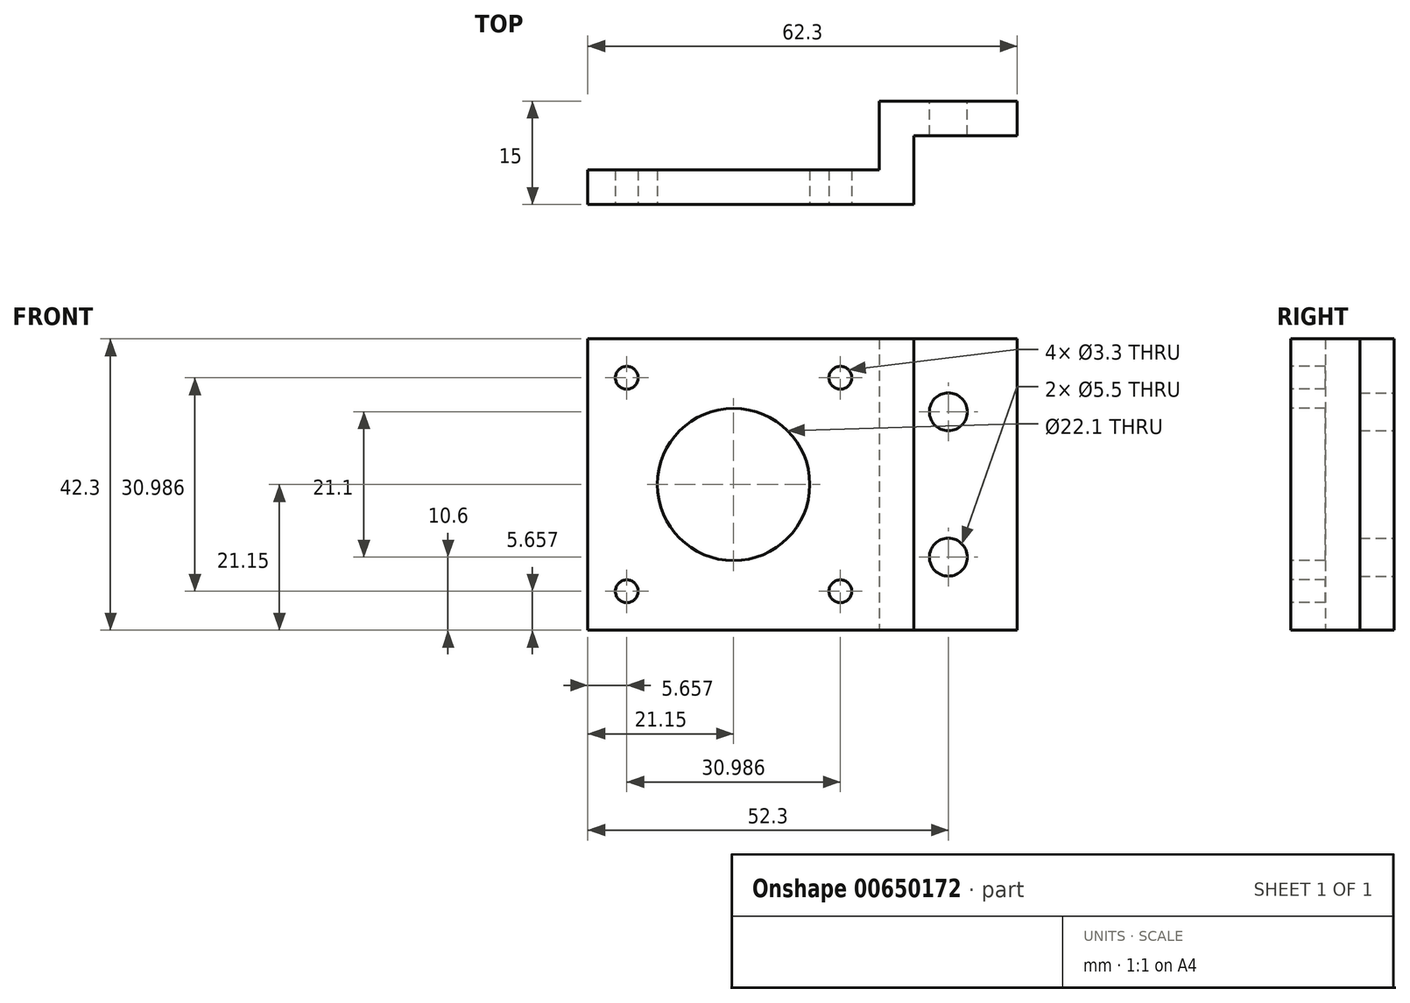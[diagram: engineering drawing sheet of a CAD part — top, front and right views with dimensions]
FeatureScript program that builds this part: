
annotation { "Feature Type Name" : "Feature", "Feature Type Description" : "" }
export const myFeature = defineFeature(function(context is Context, id is Id, definition is map)
    precondition{}
    {
        {
            var Q0;
            Q0=qCreatedBy(makeId("Front.planeOp"),FACE);
            var sketch = newSketch(context, id + "F0", { "sketchPlane" : qUnion([Q0])});
            skLineSegment(sketch, "E0.bottom", {"start": v(10, -21.15) * mm, "end": v(-10, -21.15) * mm});
            skLineSegment(sketch, "E0.top", {"start": v(10, 21.15) * mm, "end": v(-10, 21.15) * mm});
            skLineSegment(sketch, "E0.left", {"start": v(10, -21.15) * mm, "end": v(10, 21.15) * mm});
            skLineSegment(sketch, "E0.right", {"start": v(-10, -21.15) * mm, "end": v(-10, 21.15) * mm});
            skPoint(sketch, "E0.middle", {"position": v(0, 0) * mm});
            skPoint(sketch, "E1", {"position": v(0, 10.55) * mm});
            skPoint(sketch, "E2", {"position": v(0, -10.55) * mm});
            skSolve(sketch);
        }
        {
            var Q0;
            Q0=makeQuery(id+"F0.imprint","IMPRINT",FACE,{"disambiguationData":[TD([[makeQuery(id+"F0.imprint","IMPRINT",EDGE,{"derivedFrom":sQuery(id+"F0.wireOp",EDGE,"E0.bottom")}),-1.0]])]});
            extrude(context, id + "F1", {"entities" : qUnion([Q0]), "depth" : 5 * mm, "offsetDistance" : 25 * mm});
        }
        {
            var Q0;
            Q0=makeQuery(id+"F1.opExtrude","CAP_FACE",FACE,{"disambiguationData":[OSD([sQuery(id+"F0.wireOp",EDGE,"E0.bottom"),sQuery(id+"F0.wireOp",EDGE,"E0.top"),sQuery(id+"F0.wireOp",EDGE,"E0.left"),sQuery(id+"F0.wireOp",EDGE,"E0.right")])],"isStart":false});
            var sketch = newSketch(context, id + "F2", { "sketchPlane" : qUnion([Q0])});
            skLineSegment(sketch, "E3.bottom", {"start": v(-10, 21.15) * mm, "end": v(-5, 21.15) * mm});
            skLineSegment(sketch, "E3.top", {"start": v(-10, -21.15) * mm, "end": v(-5, -21.15) * mm});
            skLineSegment(sketch, "E3.left", {"start": v(-10, 21.15) * mm, "end": v(-10, -21.15) * mm});
            skLineSegment(sketch, "E3.right", {"start": v(-5, 21.15) * mm, "end": v(-5, -21.15) * mm});
            skSolve(sketch);
        }
        {
            var Q0;
            Q0=makeQuery(id+"F2.imprint","IMPRINT",FACE,{"disambiguationData":[TD([[makeQuery(id+"F2.imprint","IMPRINT",EDGE,{"derivedFrom":sQuery(id+"F2.wireOp",EDGE,"E3.bottom")}),1.0]])]});
            extrude(context, id + "F3", {"entities" : qUnion([Q0]), "operationType" : NewBodyOperationType.ADD, "depth" : 10 * mm, "offsetDistance" : 25 * mm});
        }
        {
            var Q0;
            Q0=makeQuery(id+"F3.boolean.opBoolean","MERGE",FACE,{"derivedFrom":[makeQuery(id+"F1.opExtrude","SWEPT_FACE",FACE,{"disambiguationData":[OSD([sQuery(id+"F0.wireOp",EDGE,"E0.right")])]}),makeQuery(id+"F3.opExtrude","SWEPT_FACE",FACE,{"disambiguationData":[OSD([sQuery(id+"F2.wireOp",EDGE,"E3.left")])]})]});
            var sketch = newSketch(context, id + "F4", { "sketchPlane" : qUnion([Q0])});
            skLineSegment(sketch, "E4.bottom", {"start": v(15, 21.15) * mm, "end": v(10, 21.15) * mm});
            skLineSegment(sketch, "E4.top", {"start": v(15, -21.15) * mm, "end": v(10, -21.15) * mm});
            skLineSegment(sketch, "E4.left", {"start": v(15, 21.15) * mm, "end": v(15, -21.15) * mm});
            skLineSegment(sketch, "E4.right", {"start": v(10, 21.15) * mm, "end": v(10, -21.15) * mm});
            skSolve(sketch);
        }
        {
            var Q0;
            Q0=makeQuery(id+"F4.imprint","IMPRINT",FACE,{"disambiguationData":[TD([[makeQuery(id+"F4.imprint","IMPRINT",EDGE,{"derivedFrom":sQuery(id+"F4.wireOp",EDGE,"E4.bottom")}),1.0]])]});
            extrude(context, id + "F5", {"entities" : qUnion([Q0]), "operationType" : NewBodyOperationType.ADD, "depth" : 42.3 * mm, "offsetDistance" : 25 * mm});
        }
        {
            var Q0;
            Q0=makeQuery(id+"F5.boolean.opBoolean","MERGE",FACE,{"derivedFrom":[makeQuery(id+"F3.opExtrude","CAP_FACE",FACE,{"disambiguationData":[OSD([sQuery(id+"F2.wireOp",EDGE,"E3.bottom"),sQuery(id+"F2.wireOp",EDGE,"E3.top"),sQuery(id+"F2.wireOp",EDGE,"E3.left"),sQuery(id+"F2.wireOp",EDGE,"E3.right")])],"isStart":false}),makeQuery(id+"F5.opExtrude","SWEPT_FACE",FACE,{"disambiguationData":[OSD([sQuery(id+"F4.wireOp",EDGE,"E4.left")])]})]});
            var sketch = newSketch(context, id + "F6", { "sketchPlane" : qUnion([Q0])});
            skLineSegment(sketch, "E5.bottom", {"start": v(-52.3, 21.15) * mm, "end": v(-10, 21.15) * mm});
            skLineSegment(sketch, "E5.top", {"start": v(-52.3, -21.15) * mm, "end": v(-10, -21.15) * mm});
            skLineSegment(sketch, "E5.left", {"start": v(-52.3, 21.15) * mm, "end": v(-52.3, -21.15) * mm});
            skLineSegment(sketch, "E5.right", {"start": v(-10, 21.15) * mm, "end": v(-10, -21.15) * mm});
            skPoint(sketch, "E6", {"position": v(-31.15, 0) * mm});
            skCircle(sketch, "E7", {"center": v(-31.15, 0) * mm, "radius": 11.05 * mm});
            skLineSegment(sketch, "E8", {"start": v(-52.3, 21.15) * mm, "end": v(-46.64, 15.5) * mm});
            skPoint(sketch, "E9", {"position": v(-46.64, 15.5) * mm});
            skLineSegment(sketch, "E10", {"start": v(-10, 21.15) * mm, "end": v(-15.66, 15.5) * mm});
            skLineSegment(sketch, "E11", {"start": v(-52.3, -21.15) * mm, "end": v(-46.64, -15.5) * mm});
            skLineSegment(sketch, "E12", {"start": v(-10, -21.15) * mm, "end": v(-15.66, -15.5) * mm});
            skPoint(sketch, "E13", {"position": v(-15.66, 15.5) * mm});
            skPoint(sketch, "E14", {"position": v(-15.66, -15.5) * mm});
            skPoint(sketch, "E15", {"position": v(-46.64, -15.5) * mm});
            skSolve(sketch);
        }
        {
            var Q0;
            Q0=makeQuery(id+"F6.imprint","IMPRINT",FACE,{"disambiguationData":[TD([[makeQuery(id+"F6.imprint","IMPRINT",EDGE,{"derivedFrom":sQuery(id+"F6.wireOp",EDGE,"E7")}),1.0]])]});
            extrude(context, id + "F7", {"entities" : qUnion([Q0]), "operationType" : NewBodyOperationType.REMOVE, "oppositeDirection" : true, "depth" : 5.1 * mm, "offsetDistance" : 25 * mm});
        }
        {
            var Q0;
            Q0=sQuery(id+"F6.wireOp",VERTEX,"E9");
            var Q1;
            Q1=sQuery(id+"F6.wireOp",VERTEX,"E13");
            var Q2;
            Q2=sQuery(id+"F6.wireOp",VERTEX,"E14");
            var Q3;
            Q3=sQuery(id+"F6.wireOp",VERTEX,"E15");
            var Q4;
            Q4=makeQuery(id+"F1.opExtrude","SWEPT_BODY",BODY,{"disambiguationData":[OSD([sQuery(id+"F0.wireOp",EDGE,"E0.bottom"),sQuery(id+"F0.wireOp",EDGE,"E0.top"),sQuery(id+"F0.wireOp",EDGE,"E0.left"),sQuery(id+"F0.wireOp",EDGE,"E0.right")])]});
            hole(context, id + "F8", {"style" : HoleStyle.SIMPLE, "endStyle" : HoleEndStyle.THROUGH, "standardTappedOrClearance" : lookupTablePath({ "standard" : "ISO", "fit" : "Normal", "size" : "M3", "type" : "Clearance" }), "standardBlindInLast" : lookupTablePath({ "fit" : "Standard", "standard" : "ISO", "size" : "M3", "type" : "Clearance" }), "holeDiameter" : 3.3 * mm, "majorDiameter" : 5 * mm, "isTappedThrough" : true, "tappedDepth" : 12 * mm, "tapClearance" : 3, "locations" : qUnion([Q0, Q1, Q2, Q3]), "scope" : qUnion([Q4])});
        }
        {
            var Q0;
            Q0=sQuery(id+"F0.wireOp",VERTEX,"E1");
            var Q1;
            Q1=sQuery(id+"F0.wireOp",VERTEX,"E2");
            var Q2;
            Q2=makeQuery(id+"F1.opExtrude","SWEPT_BODY",BODY,{"disambiguationData":[OSD([sQuery(id+"F0.wireOp",EDGE,"E0.bottom"),sQuery(id+"F0.wireOp",EDGE,"E0.top"),sQuery(id+"F0.wireOp",EDGE,"E0.left"),sQuery(id+"F0.wireOp",EDGE,"E0.right")])]});
            hole(context, id + "F9", {"style" : HoleStyle.SIMPLE, "endStyle" : HoleEndStyle.THROUGH, "oppositeDirection" : true, "standardTappedOrClearance" : lookupTablePath({ "standard" : "ISO", "fit" : "Normal", "size" : "M5", "type" : "Clearance" }), "standardBlindInLast" : lookupTablePath({ "fit" : "Standard", "standard" : "ISO", "size" : "M5", "type" : "Clearance" }), "holeDiameter" : 5.5 * mm, "majorDiameter" : 5 * mm, "isTappedThrough" : true, "tappedDepth" : 12 * mm, "tapClearance" : 3, "locations" : qUnion([Q0, Q1]), "scope" : qUnion([Q2])});
        }
    });
